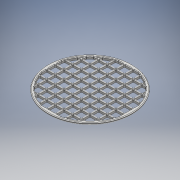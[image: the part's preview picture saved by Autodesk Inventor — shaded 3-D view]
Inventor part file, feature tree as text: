
AUTODESK INVENTOR PART (.ipt)
format: ipt  version: 2017 (Build 210142000, 142)  size: 1,989,120 bytes
history: native  units: mm
features: other x4, sketch x4, extrude x3, fillet x2, reference x2
ambient origin geometry x8: Origin, YZ Plane, XZ Plane, XY Plane, X Axis, Y Axis, Z Axis, Center Point
bodies: solido (feature_tree)
feature tree (15):
  other  "Sólido1"
  extrude  "taladros"  Depth=68.0mm
  extrude  "borde"  Depth=6.0mm
  fillet  "Empalme2"  Radius=6.0mm
  extrude  "Extrusión4"  TaperAngle=0.0deg  [1 undecoded]
  fillet  "Empalme3"  Radius=64.0mm
  sketch  "Boceto1"  dims[d0=70.0mm d1=68.0mm]
  reference  "Referencia1"
  reference  "Referencia2"
  sketch  "Boceto3"  dims[d3=4.0mm d4=0.0mm d20=6.0mm d21=6.0mm]
  sketch  "Boceto4"  dims[d22=60.0mm d24=7.0mm d25=60.0mm d27=7.0mm d30=0.0mm d31=0.0mm d32=64.0mm]
  sketch  "Boceto5"  dims[d33=68.0mm d34=4.0mm d35=0.0mm d37=0.5mm d38=0.5mm d39=0.0mm d40=0.0mm d41=1.25mm]
  other  "<userpath>\Dropbox\3D_print\diseños_PROPIOS\soap_box\conjunto.iam"
  other  "conjunto.iam"
  other  "box:1"
note: 1 required parameter value undecoded (feature->parameter linkage not recoverable at this tier; creation-order binding heuristic only, values carry confidence <= 0.55)
